FCSTD DOCUMENT  (FreeCAD 0.20R29410 (Git))
Label: ReLoki_PCB_SolderPasteJig
License: All rights reserved
LicenseURL: http://en.wikipedia.org/wiki/All_rights_reserved
objects: Part::FeaturePython×2, PartDesign::CoordinateSystem×1, App::Part×1, Sketcher::SketchObject×1
note: 4 computed .brp shape members not serialized (recipe doc carries the construction recipe); baked Part::Feature solids carry a one-line shape summary decoded from their .brp

FEATURE [PartDesign::CoordinateSystem] a2pLCS
  AttacherType = Attacher::AttachEngine3D
FEATURE [Part::FeaturePython] b_LCS_Collection_  label="LCS_Collection"  # WARN: FeaturePython — macro-defined, semantics opaque (R4)
  Group = -> [a2pLCS]
  Owner = b_ReLoki_PCB_001_
FEATURE [Part::FeaturePython] b_ReLoki_PCB_001_  label="ReLoki_PCB_001"  # a2plus imported part (geometry in sourceFile) (typed FeaturePython)
  a2p_Version = 0.4.60d
  fixedPosition = true
  lcsLink = -> [b_LCS_Collection_]
  objectType = a2pPart
  sourceFile = ./ReLoki_PCB.FCStd
  subassemblyImport = false
  timeLastImport = 1.66871e+09
  updateColors = true
FEATURE [App::Part] Part  label="Base"
  Origin = -> Origin
FEATURE [Sketcher::SketchObject] Sketch
  FullyConstrained = true
  MapMode = 2
  Support = -> [Part]
